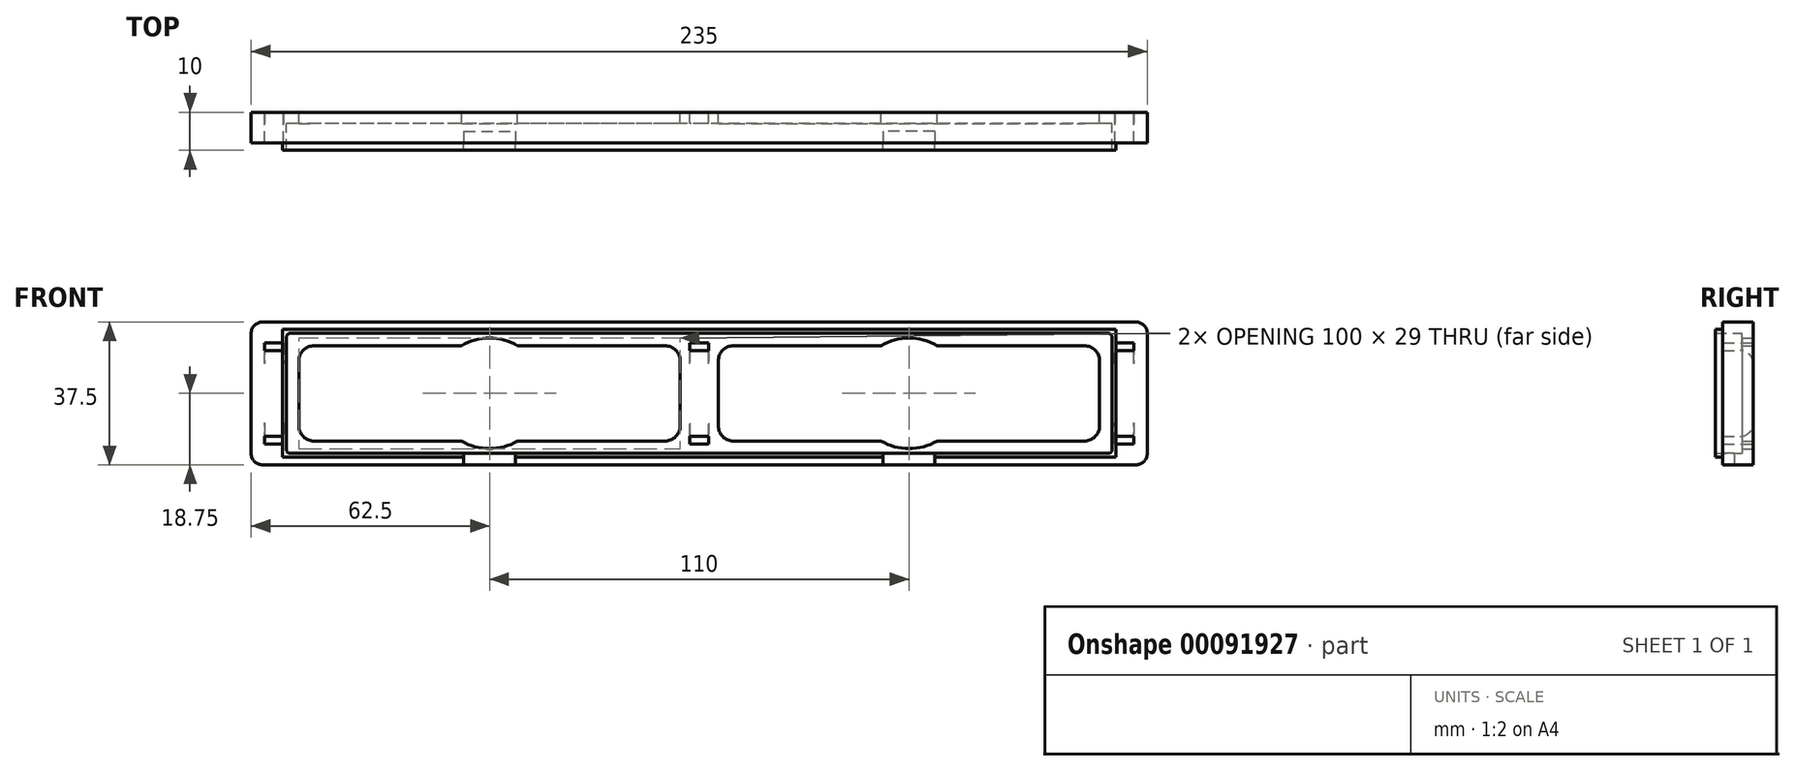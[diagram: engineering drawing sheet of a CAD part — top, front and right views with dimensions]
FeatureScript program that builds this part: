
annotation { "Feature Type Name" : "Feature", "Feature Type Description" : "" }
export const myFeature = defineFeature(function(context is Context, id is Id, definition is map)
    precondition{}
    {
        {
            var Q0;
            Q0=qCreatedBy(makeId("Front.planeOp"),FACE);
            var sketch = newSketch(context, id + "F0", { "sketchPlane" : qUnion([Q0])});
            skLineSegment(sketch, "E0.bottom", {"start": v(114.5, 18.75) * mm, "end": v(-114.5, 18.75) * mm});
            skLineSegment(sketch, "E0.top", {"start": v(114.5, -18.75) * mm, "end": v(-114.5, -18.75) * mm});
            skLineSegment(sketch, "E0.left", {"start": v(117.5, 15.75) * mm, "end": v(117.5, -15.75) * mm});
            skLineSegment(sketch, "E0.right", {"start": v(-117.5, 15.75) * mm, "end": v(-117.5, -15.75) * mm});
            skPoint(sketch, "E0.middle", {"position": v(0, 0) * mm});
            skLineSegment(sketch, "E1.bottom", {"start": v(-9, 12.5) * mm, "end": v(-101, 12.5) * mm});
            skLineSegment(sketch, "E1.top", {"start": v(-9, -12.5) * mm, "end": v(-101, -12.5) * mm});
            skLineSegment(sketch, "E1.left", {"start": v(-5, 8.5) * mm, "end": v(-5, -8.5) * mm});
            skLineSegment(sketch, "E1.right", {"start": v(-105, 8.5) * mm, "end": v(-105, -8.5) * mm});
            skPoint(sketch, "E1.middle", {"position": v(-55, 0) * mm});
            skPoint(sketch, "E2.visualSharp", {"position": v(-105, 12.5) * mm});
            skArc(sketch, "E2.filletArc", {"start": v(-101, 12.5) * mm, "mid": v(-103.83, 11.33) * mm, "end": v(-105, 8.5) * mm});
            skPoint(sketch, "E3.visualSharp", {"position": v(-5, 12.5) * mm});
            skArc(sketch, "E3.filletArc", {"start": v(-5, 8.5) * mm, "mid": v(-6.17, 11.33) * mm, "end": v(-9, 12.5) * mm});
            skPoint(sketch, "E4.visualSharp", {"position": v(-5, -12.5) * mm});
            skArc(sketch, "E4.filletArc", {"start": v(-9, -12.5) * mm, "mid": v(-6.17, -11.33) * mm, "end": v(-5, -8.5) * mm});
            skPoint(sketch, "E5.visualSharp", {"position": v(-105, -12.5) * mm});
            skArc(sketch, "E5.filletArc", {"start": v(-105, -8.5) * mm, "mid": v(-103.83, -11.33) * mm, "end": v(-101, -12.5) * mm});
            skArc(sketch, "E6.MirrorCS", {"start": v(101, 12.5) * mm, "mid": v(103.83, 11.33) * mm, "end": v(105, 8.5) * mm});
            skArc(sketch, "E7.MirrorCS", {"start": v(5, 8.5) * mm, "mid": v(6.17, 11.33) * mm, "end": v(9, 12.5) * mm});
            skArc(sketch, "E8.MirrorCS", {"start": v(9, -12.5) * mm, "mid": v(6.17, -11.33) * mm, "end": v(5, -8.5) * mm});
            skArc(sketch, "E9.MirrorCS", {"start": v(105, -8.5) * mm, "mid": v(103.83, -11.33) * mm, "end": v(101, -12.5) * mm});
            skLineSegment(sketch, "E10.MirrorCS", {"start": v(9, -12.5) * mm, "end": v(101, -12.5) * mm});
            skPoint(sketch, "E11.MirrorP", {"position": v(105, -12.5) * mm});
            skLineSegment(sketch, "E12.MirrorCS", {"start": v(5, 8.5) * mm, "end": v(5, -8.5) * mm});
            skLineSegment(sketch, "E13.MirrorCS", {"start": v(9, 12.5) * mm, "end": v(101, 12.5) * mm});
            skLineSegment(sketch, "E14.MirrorCS", {"start": v(105, 8.5) * mm, "end": v(105, -8.5) * mm});
            skPoint(sketch, "E15.MirrorP", {"position": v(5, 12.5) * mm});
            skPoint(sketch, "E16.MirrorP", {"position": v(105, 12.5) * mm});
            skPoint(sketch, "E17.MirrorP", {"position": v(55, 0) * mm});
            skPoint(sketch, "E18.MirrorP", {"position": v(5, -12.5) * mm});
            skCircle(sketch, "E19", {"center": v(-55, 0) * mm, "radius": 14.5 * mm});
            skCircle(sketch, "E20.MirrorC", {"center": v(55, 0) * mm, "radius": 14.5 * mm});
            skLineSegment(sketch, "E21.bottom", {"start": v(2.5, 11.25) * mm, "end": v(-2.5, 11.25) * mm});
            skLineSegment(sketch, "E21.top", {"start": v(2.5, 13.25) * mm, "end": v(-2.5, 13.25) * mm});
            skLineSegment(sketch, "E21.left", {"start": v(2.5, 11.25) * mm, "end": v(2.5, 13.25) * mm});
            skLineSegment(sketch, "E21.right", {"start": v(-2.5, 11.25) * mm, "end": v(-2.5, 13.25) * mm});
            skPoint(sketch, "E21.middle", {"position": v(0, 12.25) * mm});
            skLineSegment(sketch, "E22.MirrorCS", {"start": v(-2.5, -11.25) * mm, "end": v(-2.5, -13.25) * mm});
            skLineSegment(sketch, "E23.MirrorCS", {"start": v(2.5, -11.25) * mm, "end": v(-2.5, -11.25) * mm});
            skPoint(sketch, "E24.MirrorP", {"position": v(0, -12.25) * mm});
            skLineSegment(sketch, "E25.MirrorCS", {"start": v(2.5, -11.25) * mm, "end": v(2.5, -13.25) * mm});
            skLineSegment(sketch, "E26.MirrorCS", {"start": v(2.5, -13.25) * mm, "end": v(-2.5, -13.25) * mm});
            skPoint(sketch, "E27.visualSharp", {"position": v(-117.5, 18.75) * mm});
            skArc(sketch, "E27.filletArc", {"start": v(-114.5, 18.75) * mm, "mid": v(-116.62, 17.87) * mm, "end": v(-117.5, 15.75) * mm});
            skPoint(sketch, "E28.visualSharp", {"position": v(-117.5, -18.75) * mm});
            skArc(sketch, "E28.filletArc", {"start": v(-117.5, -15.75) * mm, "mid": v(-116.62, -17.87) * mm, "end": v(-114.5, -18.75) * mm});
            skPoint(sketch, "E29.visualSharp", {"position": v(117.5, -18.75) * mm});
            skArc(sketch, "E29.filletArc", {"start": v(114.5, -18.75) * mm, "mid": v(116.62, -17.87) * mm, "end": v(117.5, -15.75) * mm});
            skPoint(sketch, "E30.visualSharp", {"position": v(117.5, 18.75) * mm});
            skArc(sketch, "E30.filletArc", {"start": v(117.5, 15.75) * mm, "mid": v(116.62, 17.87) * mm, "end": v(114.5, 18.75) * mm});
            skLineSegment(sketch, "E31.bottom", {"start": v(-109, 13.25) * mm, "end": v(-114, 13.25) * mm});
            skLineSegment(sketch, "E31.top", {"start": v(-109, 11.25) * mm, "end": v(-114, 11.25) * mm});
            skLineSegment(sketch, "E31.left", {"start": v(-109, 13.25) * mm, "end": v(-109, 11.25) * mm});
            skLineSegment(sketch, "E31.right", {"start": v(-114, 13.25) * mm, "end": v(-114, 11.25) * mm});
            skPoint(sketch, "E31.middle", {"position": v(-111.5, 12.25) * mm});
            skPoint(sketch, "E32.MirrorP", {"position": v(-111.5, -12.25) * mm});
            skLineSegment(sketch, "E33.MirrorCS", {"start": v(-114, -13.25) * mm, "end": v(-114, -11.25) * mm});
            skLineSegment(sketch, "E34.MirrorCS", {"start": v(-109, -11.25) * mm, "end": v(-114, -11.25) * mm});
            skLineSegment(sketch, "E35.MirrorCS", {"start": v(-109, -13.25) * mm, "end": v(-109, -11.25) * mm});
            skLineSegment(sketch, "E36.MirrorCS", {"start": v(-109, -13.25) * mm, "end": v(-114, -13.25) * mm});
            skLineSegment(sketch, "E37.MirrorCS", {"start": v(109, -13.25) * mm, "end": v(109, -11.25) * mm});
            skLineSegment(sketch, "E38.MirrorCS", {"start": v(114, 13.25) * mm, "end": v(114, 11.25) * mm});
            skLineSegment(sketch, "E39.MirrorCS", {"start": v(114, -13.25) * mm, "end": v(114, -11.25) * mm});
            skLineSegment(sketch, "E40.MirrorCS", {"start": v(109, 13.25) * mm, "end": v(109, 11.25) * mm});
            skLineSegment(sketch, "E41.MirrorCS", {"start": v(109, 13.25) * mm, "end": v(114, 13.25) * mm});
            skLineSegment(sketch, "E42.MirrorCS", {"start": v(109, -13.25) * mm, "end": v(114, -13.25) * mm});
            skLineSegment(sketch, "E43.MirrorCS", {"start": v(109, 11.25) * mm, "end": v(114, 11.25) * mm});
            skLineSegment(sketch, "E44.MirrorCS", {"start": v(109, -11.25) * mm, "end": v(114, -11.25) * mm});
            skPoint(sketch, "E45.MirrorP", {"position": v(111.5, 12.25) * mm});
            skPoint(sketch, "E46.MirrorP", {"position": v(111.5, -12.25) * mm});
            skSolve(sketch);
        }
        {
            var Q0;
            Q0=qSketchRegion(id+"F0",true);
            extrude(context, id + "F1", {"entities" : qUnion([Q0]), "depth" : 3 * mm});
        }
        {
            var Q0;
            Q0=makeQuery(id+"F1.opExtrude","CAP_FACE",FACE,{"disambiguationData":[OSD([sQuery(id+"F0.wireOp",EDGE,"E0.bottom"),sQuery(id+"F0.wireOp",EDGE,"E0.top"),sQuery(id+"F0.wireOp",EDGE,"E0.left"),sQuery(id+"F0.wireOp",EDGE,"E0.right"),sQuery(id+"F0.wireOp",EDGE,"E1.bottom"),sQuery(id+"F0.wireOp",EDGE,"E1.top"),sQuery(id+"F0.wireOp",EDGE,"E1.left"),sQuery(id+"F0.wireOp",EDGE,"E1.right"),sQuery(id+"F0.wireOp",EDGE,"E2.filletArc"),sQuery(id+"F0.wireOp",EDGE,"E3.filletArc"),sQuery(id+"F0.wireOp",EDGE,"E4.filletArc"),sQuery(id+"F0.wireOp",EDGE,"E5.filletArc"),sQuery(id+"F0.wireOp",EDGE,"E6.MirrorCS"),sQuery(id+"F0.wireOp",EDGE,"E7.MirrorCS"),sQuery(id+"F0.wireOp",EDGE,"E8.MirrorCS"),sQuery(id+"F0.wireOp",EDGE,"E9.MirrorCS"),sQuery(id+"F0.wireOp",EDGE,"E10.MirrorCS"),sQuery(id+"F0.wireOp",EDGE,"E12.MirrorCS"),sQuery(id+"F0.wireOp",EDGE,"E13.MirrorCS"),sQuery(id+"F0.wireOp",EDGE,"E14.MirrorCS")])],"isStart":false});
            var sketch = newSketch(context, id + "F2", { "sketchPlane" : qUnion([Q0])});
            skLineSegment(sketch, "E47.bottom", {"start": v(107.25, 15.75) * mm, "end": v(-107.25, 15.75) * mm});
            skLineSegment(sketch, "E47.top", {"start": v(107.25, -15.75) * mm, "end": v(-107.25, -15.75) * mm});
            skLineSegment(sketch, "E47.left", {"start": v(108.25, 14.75) * mm, "end": v(108.25, -14.75) * mm});
            skLineSegment(sketch, "E47.right", {"start": v(-108.25, 14.75) * mm, "end": v(-108.25, -14.75) * mm});
            skPoint(sketch, "E48.visualSharp", {"position": v(-108.25, 15.75) * mm});
            skArc(sketch, "E48.filletArc", {"start": v(-107.25, 15.75) * mm, "mid": v(-107.96, 15.46) * mm, "end": v(-108.25, 14.75) * mm});
            skPoint(sketch, "E49.visualSharp", {"position": v(108.25, 15.75) * mm});
            skArc(sketch, "E49.filletArc", {"start": v(108.25, 14.75) * mm, "mid": v(107.96, 15.46) * mm, "end": v(107.25, 15.75) * mm});
            skPoint(sketch, "E50.visualSharp", {"position": v(108.25, -15.75) * mm});
            skArc(sketch, "E50.filletArc", {"start": v(107.25, -15.75) * mm, "mid": v(107.96, -15.46) * mm, "end": v(108.25, -14.75) * mm});
            skPoint(sketch, "E51.visualSharp", {"position": v(-108.25, -15.75) * mm});
            skArc(sketch, "E51.filletArc", {"start": v(-108.25, -14.75) * mm, "mid": v(-107.96, -15.46) * mm, "end": v(-107.25, -15.75) * mm});
            skSolve(sketch);
        }
        {
            var Q0;
            Q0=makeQuery(id+"F2.imprint","IMPRINT",FACE,{"disambiguationData":[TD([[makeQuery(id+"F2.imprint","IMPRINT",EDGE,{"derivedFrom":sQuery(id+"F2.wireOp",EDGE,"E47.bottom")}),-1.0]])]});
            var Q1;
            Q1=makeQuery(id+"F2.imprint","IMPRINT",FACE,{"disambiguationData":[TD([[makeQuery(id+"F2.imprint","IMPRINT",EDGE,{"derivedFrom":sQuery(id+"F2.wireOp",EDGE,"8UQ35Aj4-GzFw-aaHB-QqC8-tIVl76PQ1ExV")}),1.0]])]});
            extrude(context, id + "F3", {"entities" : qUnion([Q0, Q1]), "operationType" : NewBodyOperationType.ADD, "depth" : 5 * mm});
        }
        {
            var Q0;
            Q0=makeQuery(id+"F3.opExtrude","CAP_FACE",FACE,{"disambiguationData":[OSD([sQuery(id+"F0.wireOp",EDGE,"E0.bottom"),sQuery(id+"F0.wireOp",EDGE,"E0.top"),sQuery(id+"F0.wireOp",EDGE,"E0.left"),sQuery(id+"F0.wireOp",EDGE,"E0.right"),sQuery(id+"F0.wireOp",EDGE,"ZHHTkMPx-xk2V-YnWK-Tyof-4nBsazcNe8Yu"),sQuery(id+"F0.wireOp",EDGE,"0744b17f-897b-458e-b34b-7ca158b34d090.MirrorCS"),sQuery(id+"F2.wireOp",EDGE,"E47.bottom"),sQuery(id+"F2.wireOp",EDGE,"E47.top"),sQuery(id+"F2.wireOp",EDGE,"E47.left"),sQuery(id+"F2.wireOp",EDGE,"E47.right"),sQuery(id+"F2.wireOp",EDGE,"E48.filletArc"),sQuery(id+"F2.wireOp",EDGE,"E49.filletArc"),sQuery(id+"F2.wireOp",EDGE,"E50.filletArc"),sQuery(id+"F2.wireOp",EDGE,"E51.filletArc"),sQuery(id+"F2.wireOp",EDGE,"21LFbrld-Wxhg-M3QD-jiVL-tybxt2T7NddJ"),sQuery(id+"F2.wireOp",EDGE,"745e8d08-7811-4726-80f7-b7a76f0ceae30.MirrorC")])],"isStart":false});
            var sketch = newSketch(context, id + "F4", { "sketchPlane" : qUnion([Q0])});
            skLineSegment(sketch, "E52.bottom", {"start": v(-109.25, 16.75) * mm, "end": v(109.25, 16.75) * mm});
            skLineSegment(sketch, "E52.top", {"start": v(-109.25, -16.75) * mm, "end": v(109.25, -16.75) * mm});
            skLineSegment(sketch, "E52.left", {"start": v(-109.25, 16.75) * mm, "end": v(-109.25, -16.75) * mm});
            skLineSegment(sketch, "E52.right", {"start": v(109.25, 16.75) * mm, "end": v(109.25, -16.75) * mm});
            skPoint(sketch, "E52.middle", {"position": v(0, 0) * mm});
            skLineSegment(sketch, "E53.bottom", {"start": v(-107.25, 15.75) * mm, "end": v(107.25, 15.75) * mm});
            skLineSegment(sketch, "E53.top", {"start": v(-107.25, -15.75) * mm, "end": v(107.25, -15.75) * mm});
            skLineSegment(sketch, "E53.left", {"start": v(-108.25, 14.75) * mm, "end": v(-108.25, -14.75) * mm});
            skLineSegment(sketch, "E53.right", {"start": v(108.25, 14.75) * mm, "end": v(108.25, -14.75) * mm});
            skPoint(sketch, "E54.visualSharp", {"position": v(-108.25, 15.75) * mm});
            skArc(sketch, "E54.filletArc", {"start": v(-107.25, 15.75) * mm, "mid": v(-107.96, 15.46) * mm, "end": v(-108.25, 14.75) * mm});
            skPoint(sketch, "E55.visualSharp", {"position": v(-108.25, -15.75) * mm});
            skArc(sketch, "E55.filletArc", {"start": v(-108.25, -14.75) * mm, "mid": v(-107.96, -15.46) * mm, "end": v(-107.25, -15.75) * mm});
            skPoint(sketch, "E56.visualSharp", {"position": v(108.25, 15.75) * mm});
            skArc(sketch, "E56.filletArc", {"start": v(108.25, 14.75) * mm, "mid": v(107.96, 15.46) * mm, "end": v(107.25, 15.75) * mm});
            skPoint(sketch, "E57.visualSharp", {"position": v(108.25, -15.75) * mm});
            skArc(sketch, "E57.filletArc", {"start": v(107.25, -15.75) * mm, "mid": v(107.96, -15.46) * mm, "end": v(108.25, -14.75) * mm});
            skSolve(sketch);
        }
        {
            var Q0;
            Q0=qSketchRegion(id+"F4",true);
            extrude(context, id + "F5", {"entities" : qUnion([Q0]), "operationType" : NewBodyOperationType.ADD, "depth" : 2 * mm});
        }
        {
            var Q0;
            {var subQ0=sQuery(id+"F0.wireOp",EDGE,"E0.top");Q0=makeQuery(id+"F3.boolean.opBoolean","MERGE",FACE,{"derivedFrom":[makeQuery(id+"F1.opExtrude","SWEPT_FACE",FACE,{"disambiguationData":[OSD([subQ0])]}),makeQuery(id+"F3.opExtrude","SWEPT_FACE",FACE,{"disambiguationData":[OSD([subQ0])]})]});}
            var sketch = newSketch(context, id + "F6", { "sketchPlane" : qUnion([Q0])});
            skLineSegment(sketch, "E58.bottom", {"start": v(-61.75, 5) * mm, "end": v(-48.25, 5) * mm});
            skLineSegment(sketch, "E58.top", {"start": v(-61.75, 10) * mm, "end": v(-48.25, 10) * mm});
            skLineSegment(sketch, "E58.left", {"start": v(-61.75, 5) * mm, "end": v(-61.75, 10) * mm});
            skLineSegment(sketch, "E58.right", {"start": v(-48.25, 5) * mm, "end": v(-48.25, 10) * mm});
            skPoint(sketch, "E59", {"position": v(-55, 5) * mm});
            skPoint(sketch, "E60.MirrorP", {"position": v(55, 5) * mm});
            skLineSegment(sketch, "E61.MirrorCS", {"start": v(48.25, 5) * mm, "end": v(48.25, 10) * mm});
            skLineSegment(sketch, "E62.MirrorCS", {"start": v(61.75, 5) * mm, "end": v(61.75, 10) * mm});
            skLineSegment(sketch, "E63.MirrorCS", {"start": v(61.75, 5) * mm, "end": v(48.25, 5) * mm});
            skLineSegment(sketch, "E64.MirrorCS", {"start": v(61.75, 10) * mm, "end": v(48.25, 10) * mm});
            skSolve(sketch);
        }
        {
            var Q0;
            Q0=qSketchRegion(id+"F6",true);
            extrude(context, id + "F7", {"entities" : qUnion([Q0]), "operationType" : NewBodyOperationType.REMOVE, "oppositeDirection" : true, "depth" : 25 * mm});
        }
        {
            var Q0;
            Q0=makeQuery(id+"F1.opExtrude","CAP_EDGE",EDGE,{"disambiguationData":[OSD([sQuery(id+"F0.wireOp",EDGE,"E21.bottom")])],"isStart":true});
            var Q1;
            Q1=makeQuery(id+"F1.opExtrude","CAP_EDGE",EDGE,{"disambiguationData":[OSD([sQuery(id+"F0.wireOp",EDGE,"E23.MirrorCS")])],"isStart":true});
            var Q2;
            Q2=makeQuery(id+"F1.opExtrude","CAP_EDGE",EDGE,{"disambiguationData":[OSD([sQuery(id+"F0.wireOp",EDGE,"E43.MirrorCS")])],"isStart":true});
            var Q3;
            Q3=makeQuery(id+"F1.opExtrude","CAP_EDGE",EDGE,{"disambiguationData":[OSD([sQuery(id+"F0.wireOp",EDGE,"E44.MirrorCS")])],"isStart":true});
            var Q4;
            Q4=makeQuery(id+"F1.opExtrude","CAP_EDGE",EDGE,{"disambiguationData":[OSD([sQuery(id+"F0.wireOp",EDGE,"E31.top")])],"isStart":true});
            var Q5;
            Q5=makeQuery(id+"F1.opExtrude","CAP_EDGE",EDGE,{"disambiguationData":[OSD([sQuery(id+"F0.wireOp",EDGE,"E34.MirrorCS")])],"isStart":true});
            fillet(context, id + "F8", {"entities" : qUnion([Q0, Q1, Q2, Q3, Q4, Q5]), "radius" : 3.5 * mm, "tangentPropagation" : true, "allowEdgeOverflow" : false});
        }
    });
